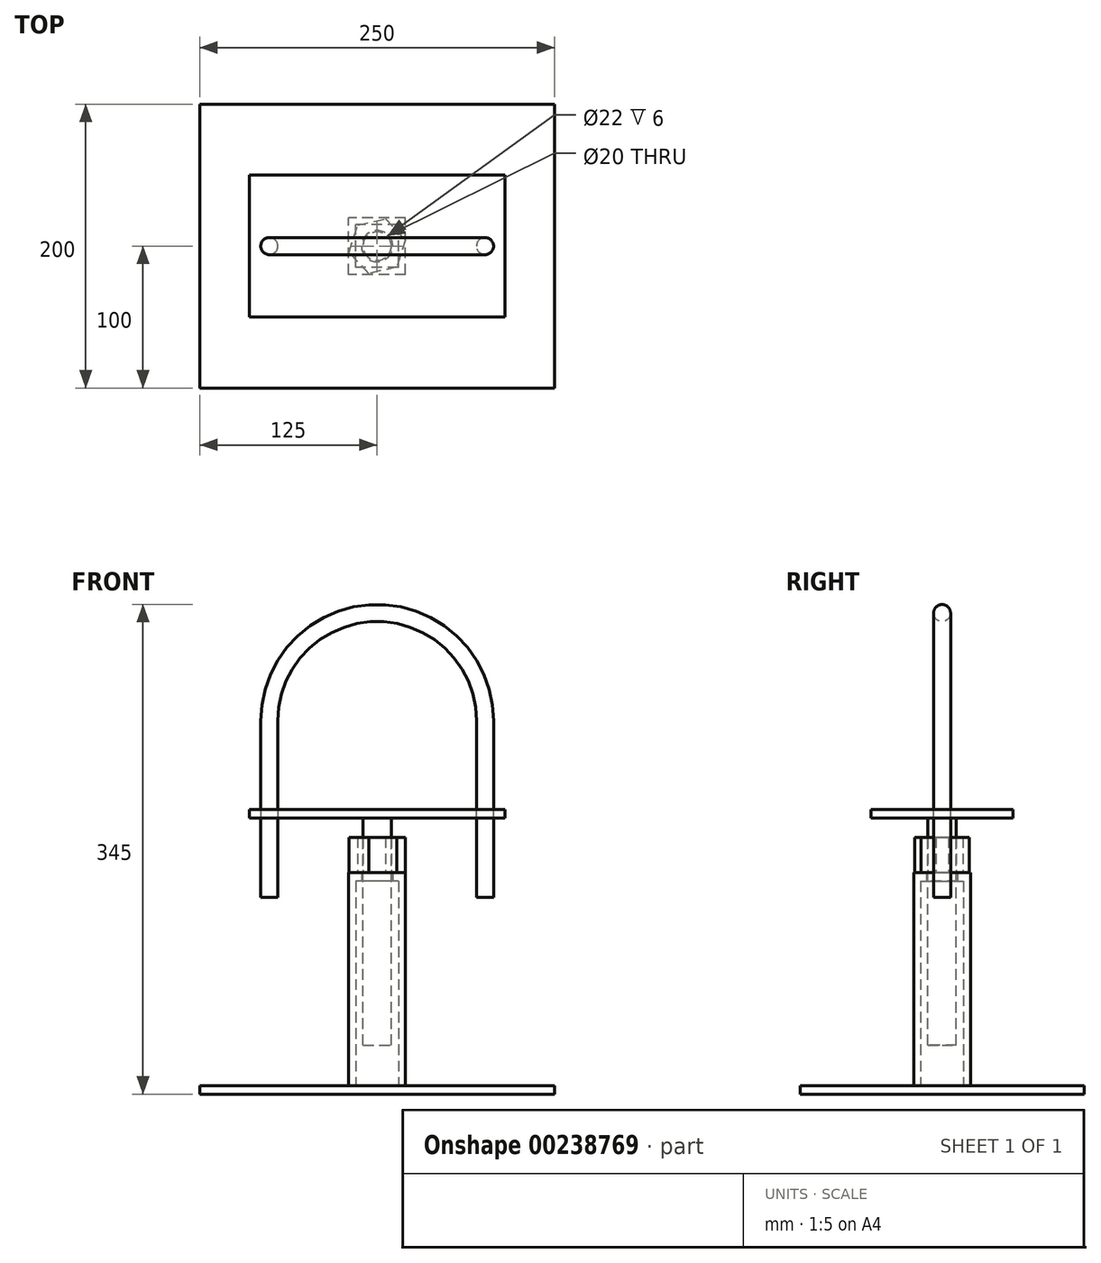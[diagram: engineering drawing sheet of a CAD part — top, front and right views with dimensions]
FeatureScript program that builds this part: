
annotation { "Feature Type Name" : "Feature", "Feature Type Description" : "" }
export const myFeature = defineFeature(function(context is Context, id is Id, definition is map)
    precondition{}
    {
        {
            var Q0;
            Q0=qCreatedBy(makeId("Top.planeOp"),FACE);
            var sketch = newSketch(context, id + "F0", { "sketchPlane" : qUnion([Q0])});
            skLineSegment(sketch, "E0.bottom", {"start": v(-125, -100) * mm, "end": v(125, -100) * mm});
            skLineSegment(sketch, "E0.top", {"start": v(-125, 100) * mm, "end": v(125, 100) * mm});
            skLineSegment(sketch, "E0.left", {"start": v(-125, -100) * mm, "end": v(-125, 100) * mm});
            skLineSegment(sketch, "E0.right", {"start": v(125, -100) * mm, "end": v(125, 100) * mm});
            skPoint(sketch, "E0.middle", {"position": v(0, 0) * mm});
            skSolve(sketch);
        }
        {
            var Q0;
            Q0 = qSketchRegion(id + "F0", true);
            extrude(context, id + "F1", {"entities" : qUnion([Q0]), "depth" : 6 * mm});
        }
        {
            var Q0;
            Q0=makeQuery(id+"F1.opExtrude","CAP_FACE",FACE,{"disambiguationData":[OSD([sQuery(id+"F0.wireOp",EDGE,"E0.bottom"),sQuery(id+"F0.wireOp",EDGE,"E0.top"),sQuery(id+"F0.wireOp",EDGE,"E0.left"),sQuery(id+"F0.wireOp",EDGE,"E0.right")])],"isStart":false});
            var sketch = newSketch(context, id + "F2", { "sketchPlane" : qUnion([Q0])});
            skLineSegment(sketch, "E1.bottom", {"start": v(20, -20) * mm, "end": v(-20, -20) * mm});
            skLineSegment(sketch, "E1.top", {"start": v(20, 20) * mm, "end": v(-20, 20) * mm});
            skLineSegment(sketch, "E1.left", {"start": v(20, -20) * mm, "end": v(20, 20) * mm});
            skLineSegment(sketch, "E1.right", {"start": v(-20, -20) * mm, "end": v(-20, 20) * mm});
            skPoint(sketch, "E1.middle", {"position": v(0, 0) * mm});
            skLineSegment(sketch, "E2.0", {"start": v(15, 15) * mm, "end": v(-15, 15) * mm});
            skLineSegment(sketch, "E3.0", {"start": v(-15, -15) * mm, "end": v(-15, 15) * mm});
            skLineSegment(sketch, "E4.0", {"start": v(15, -15) * mm, "end": v(-15, -15) * mm});
            skLineSegment(sketch, "E5.0", {"start": v(15, -15) * mm, "end": v(15, 15) * mm});
            skSolve(sketch);
        }
        {
            var Q0;
            Q0 = qSketchRegion(id + "F2", true);
            extrude(context, id + "F3", {"entities" : qUnion([Q0]), "depth" : 144 * mm});
        }
        {
            var Q0;
            Q0=makeQuery(id+"F3.opExtrude","CAP_FACE",FACE,{"disambiguationData":[OSD([sQuery(id+"F2.wireOp",EDGE,"E1.bottom"),sQuery(id+"F2.wireOp",EDGE,"E1.top"),sQuery(id+"F2.wireOp",EDGE,"E1.left"),sQuery(id+"F2.wireOp",EDGE,"E1.right"),sQuery(id+"F2.wireOp",EDGE,"E2.0"),sQuery(id+"F2.wireOp",EDGE,"E3.0"),sQuery(id+"F2.wireOp",EDGE,"E4.0"),sQuery(id+"F2.wireOp",EDGE,"E5.0")])],"isStart":false});
            var sketch = newSketch(context, id + "F4", { "sketchPlane" : qUnion([Q0])});
            skLineSegment(sketch, "E6.bottom", {"start": v(20, 20) * mm, "end": v(-20, 20) * mm});
            skLineSegment(sketch, "E6.top", {"start": v(20, -20) * mm, "end": v(-20, -20) * mm});
            skLineSegment(sketch, "E6.left", {"start": v(20, 20) * mm, "end": v(20, -20) * mm});
            skLineSegment(sketch, "E6.right", {"start": v(-20, 20) * mm, "end": v(-20, -20) * mm});
            skPoint(sketch, "E6.middle", {"position": v(0, 0) * mm});
            skCircle(sketch, "E7", {"center": v(0, 0) * mm, "radius": 11 * mm});
            skSolve(sketch);
        }
        {
            var Q0;
            Q0 = qSketchRegion(id + "F4", true);
            extrude(context, id + "F5", {"entities" : qUnion([Q0]), "operationType" : NewBodyOperationType.ADD, "depth" : 6 * mm});
        }
        {
            var Q0;
            Q0=qCreatedBy(makeId("Top.planeOp"),FACE);
            cPlane(context, id + "F6", {"entities" : qUnion([Q0]), "cplaneType" : CPlaneType.OFFSET, "offset" : 200.5 * mm, "width" : 150 * mm, "height" : 150 * mm});
        }
        {
            var Q0;
            Q0=qCreatedBy(id+"F6.planeOp",FACE);
            var sketch = newSketch(context, id + "F7", { "sketchPlane" : qUnion([Q0])});
            skLineSegment(sketch, "E8.bottom", {"start": v(-90, -50) * mm, "end": v(90, -50) * mm});
            skLineSegment(sketch, "E8.top", {"start": v(-90, 50) * mm, "end": v(90, 50) * mm});
            skLineSegment(sketch, "E8.left", {"start": v(-90, -50) * mm, "end": v(-90, 50) * mm});
            skLineSegment(sketch, "E8.right", {"start": v(90, -50) * mm, "end": v(90, 50) * mm});
            skPoint(sketch, "E8.middle", {"position": v(0, 0) * mm});
            skSolve(sketch);
        }
        {
            var Q0;
            Q0 = qSketchRegion(id + "F7", true);
            extrude(context, id + "F8", {"entities" : qUnion([Q0]), "oppositeDirection" : true, "depth" : 6 * mm});
        }
        {
            var Q0;
            Q0=makeQuery(id+"F8.opExtrude","CAP_FACE",FACE,{"disambiguationData":[OSD([sQuery(id+"F7.wireOp",EDGE,"E8.bottom"),sQuery(id+"F7.wireOp",EDGE,"E8.top"),sQuery(id+"F7.wireOp",EDGE,"E8.left"),sQuery(id+"F7.wireOp",EDGE,"E8.right")])],"isStart":false});
            var sketch = newSketch(context, id + "F9", { "sketchPlane" : qUnion([Q0])});
            skCircle(sketch, "E9", {"center": v(0, 0) * mm, "radius": 10 * mm});
            skSolve(sketch);
        }
        {
            var Q0;
            Q0 = qSketchRegion(id + "F9", true);
            extrude(context, id + "F10", {"entities" : qUnion([Q0]), "depth" : 160 * mm});
        }
        {
            var Q0;
            Q0=qCreatedBy(makeId("Front.planeOp"),FACE);
            var sketch = newSketch(context, id + "F11", { "sketchPlane" : qUnion([Q0])});
            skCircle(sketch, "E10", {"center": v(0, 263) * mm, "radius": 62.5 * mm, "construction": true});
            skLineSegment(sketch, "E11", {"start": v(0, 263) * mm, "end": v(0, -102.6) * mm, "construction": true});
            skLineSegment(sketch, "E12.0", {"start": v(-76, 263) * mm, "end": v(-76, 138.53) * mm});
            skLineSegment(sketch, "E13.0", {"start": v(76, 263) * mm, "end": v(76, 138.53) * mm});
            skArc(sketch, "E14", {"start": v(76, 263) * mm, "mid": v(0, 339) * mm, "end": v(-76, 263) * mm});
            skLineSegment(sketch, "E15", {"start": v(-142.76, 138.53) * mm, "end": v(183.19, 138.53) * mm, "construction": true});
            skSolve(sketch);
        }
        {
            var Q0;
            Q0=qCreatedBy(makeId("Top.planeOp"),FACE);
            cPlane(context, id + "F12", {"entities" : qUnion([Q0]), "cplaneType" : CPlaneType.OFFSET, "offset" : 138.53 * mm, "width" : 150 * mm, "height" : 150 * mm});
        }
        {
            var Q0;
            Q0=qCreatedBy(id+"F12.planeOp",FACE);
            var sketch = newSketch(context, id + "F13", { "sketchPlane" : qUnion([Q0])});
            skCircle(sketch, "E16", {"center": v(76, 0) * mm, "radius": 6 * mm});
            skSolve(sketch);
        }
        {
            var Q0;
            Q0=makeQuery(id+"F13.imprint","IMPRINT",FACE,{"disambiguationData":[TD([[makeQuery(id+"F13.imprint","IMPRINT",EDGE,{"derivedFrom":sQuery(id+"F13.wireOp",EDGE,"E16")}),1.0]])]});
            var Q1;
            Q1=sQuery(id+"F11.wireOp",EDGE,"E13.0");
            var Q2;
            Q2=sQuery(id+"F11.wireOp",EDGE,"E14");
            var Q3;
            Q3=sQuery(id+"F11.wireOp",EDGE,"E12.0");
            sweep(context, id + "F14", {"profiles" : qUnion([Q0]), "path" : qUnion([Q1, Q2, Q3])});
        }
        {
            var Q0;
            Q0=makeQuery(id+"F5.opExtrude","CAP_FACE",FACE,{"disambiguationData":[OSD([sQuery(id+"F4.wireOp",EDGE,"E6.bottom"),sQuery(id+"F4.wireOp",EDGE,"E6.top"),sQuery(id+"F4.wireOp",EDGE,"E6.left"),sQuery(id+"F4.wireOp",EDGE,"E6.right"),sQuery(id+"F4.wireOp",EDGE,"E7")])],"isStart":false});
            var sketch = newSketch(context, id + "F15", { "sketchPlane" : qUnion([Q0])});
            skCircle(sketch, "E17.cCircle", {"center": v(0, 0) * mm, "radius": 17.5 * mm, "construction": true});
            skLineSegment(sketch, "E17.0", {"start": v(-5.99, -19.3) * mm, "end": v(-19.7, -4.46) * mm});
            skLineSegment(sketch, "E17.1", {"start": v(-19.7, -4.46) * mm, "end": v(-13.72, 14.84) * mm});
            skLineSegment(sketch, "E17.2", {"start": v(-13.72, 14.84) * mm, "end": v(5.99, 19.3) * mm});
            skLineSegment(sketch, "E17.3", {"start": v(5.99, 19.3) * mm, "end": v(19.7, 4.46) * mm});
            skLineSegment(sketch, "E17.4", {"start": v(19.7, 4.46) * mm, "end": v(13.72, -14.84) * mm});
            skLineSegment(sketch, "E17.5", {"start": v(13.72, -14.84) * mm, "end": v(-5.99, -19.3) * mm});
            skPoint(sketch, "E17.0.midPoint", {"position": v(-12.85, -11.88) * mm});
            skCircle(sketch, "E18", {"center": v(0, 0) * mm, "radius": 10 * mm});
            skSolve(sketch);
        }
        {
            var Q0;
            Q0 = qSketchRegion(id + "F15", true);
            extrude(context, id + "F16", {"entities" : qUnion([Q0]), "depth" : 25 * mm});
        }
    });
